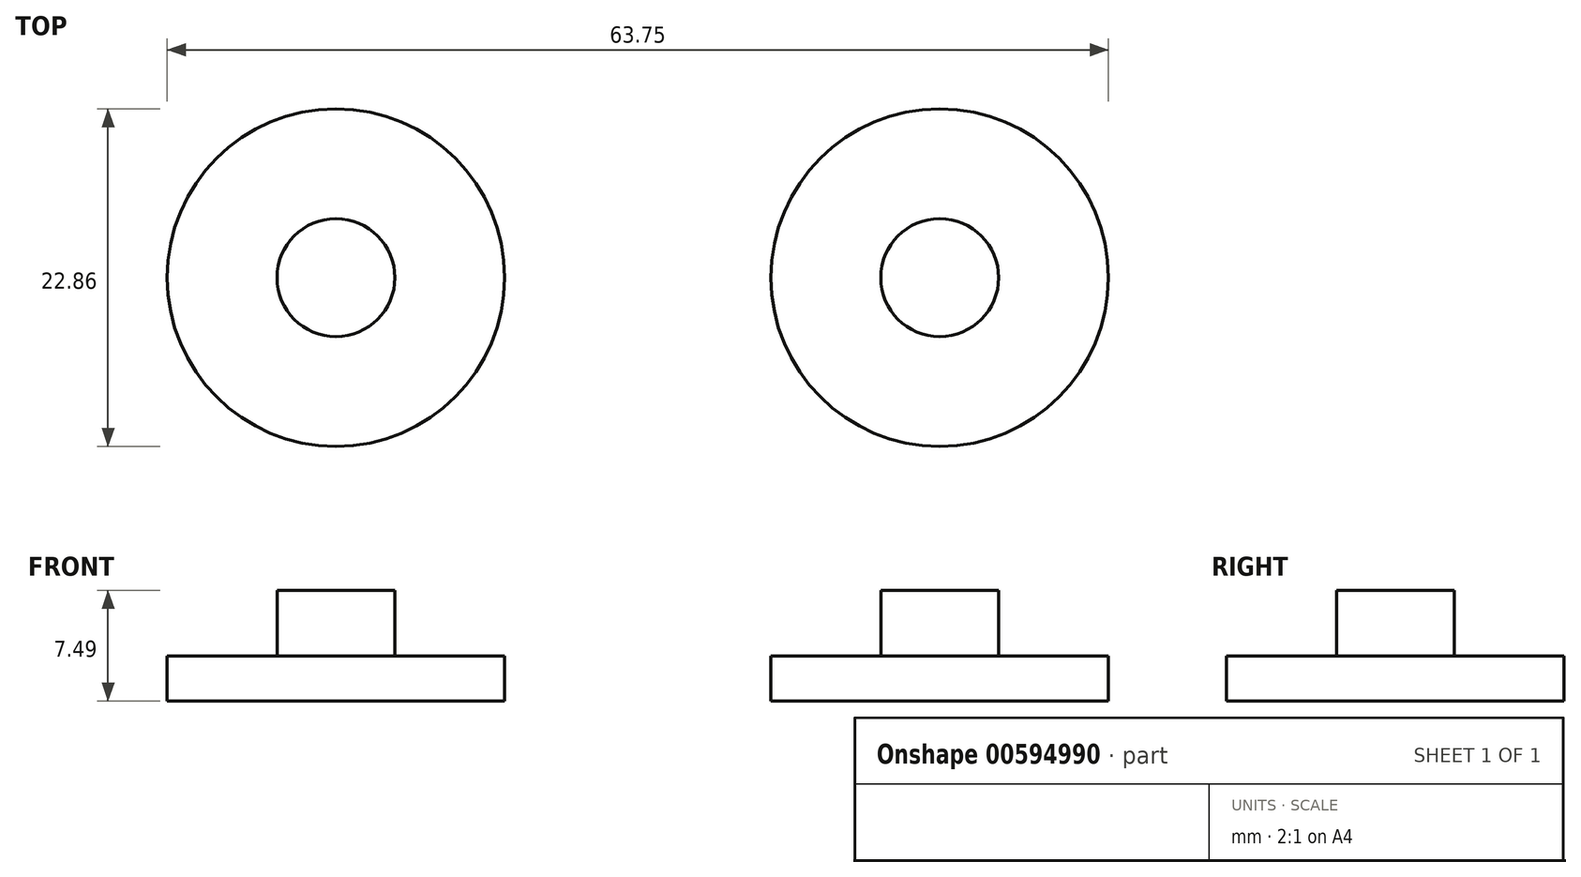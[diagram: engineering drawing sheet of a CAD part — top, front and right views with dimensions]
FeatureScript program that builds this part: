
annotation { "Feature Type Name" : "Feature", "Feature Type Description" : "" }
export const myFeature = defineFeature(function(context is Context, id is Id, definition is map)
    precondition{}
    {
        {
            var Q0;
            Q0=qCreatedBy(makeId("Top.planeOp"),FACE);
            var sketch = newSketch(context, id + "F0", { "sketchPlane" : qUnion([Q0])});
            skCircle(sketch, "E0", {"center": v(13.2, 16.31) * mm, "radius": 11.43 * mm});
            skSolve(sketch);
        }
        {
            var Q0;
            Q0 = qSketchRegion(id + "F0", true);
            extrude(context, id + "F1", {"entities" : qUnion([Q0]), "depth" : 3.05 * mm, "offsetDistance" : 25.4 * mm});
        }
        {
            var Q0;
            Q0=makeQuery(id+"F1.opExtrude","CAP_FACE",FACE,{"disambiguationData":[OSD([sQuery(id+"F0.wireOp",EDGE,"E0")])],"isStart":false});
            var sketch = newSketch(context, id + "F2", { "sketchPlane" : qUnion([Q0])});
            skCircle(sketch, "E1", {"center": v(13.2, 16.31) * mm, "radius": 4 * mm});
            skSolve(sketch);
        }
        {
            var Q0;
            Q0 = qSketchRegion(id + "F2", true);
            extrude(context, id + "F3", {"entities" : qUnion([Q0]), "operationType" : NewBodyOperationType.ADD, "depth" : 4.44 * mm, "offsetDistance" : 25.4 * mm});
        }
        {
            var Q0;
            Q0=makeQuery(id+"F1.opExtrude","SWEPT_BODY",BODY,{"disambiguationData":[OSD([sQuery(id+"F0.wireOp",EDGE,"E0")])]});
            transform(context, id + "F4", {"entities" : qUnion([Q0]), "transformType" : TransformType.TRANSLATION_3D, "dx" : -40.9 * mm, "dy" : 0 * mm, "dz" : 0 * mm, "makeCopy" : true});
        }
    });
